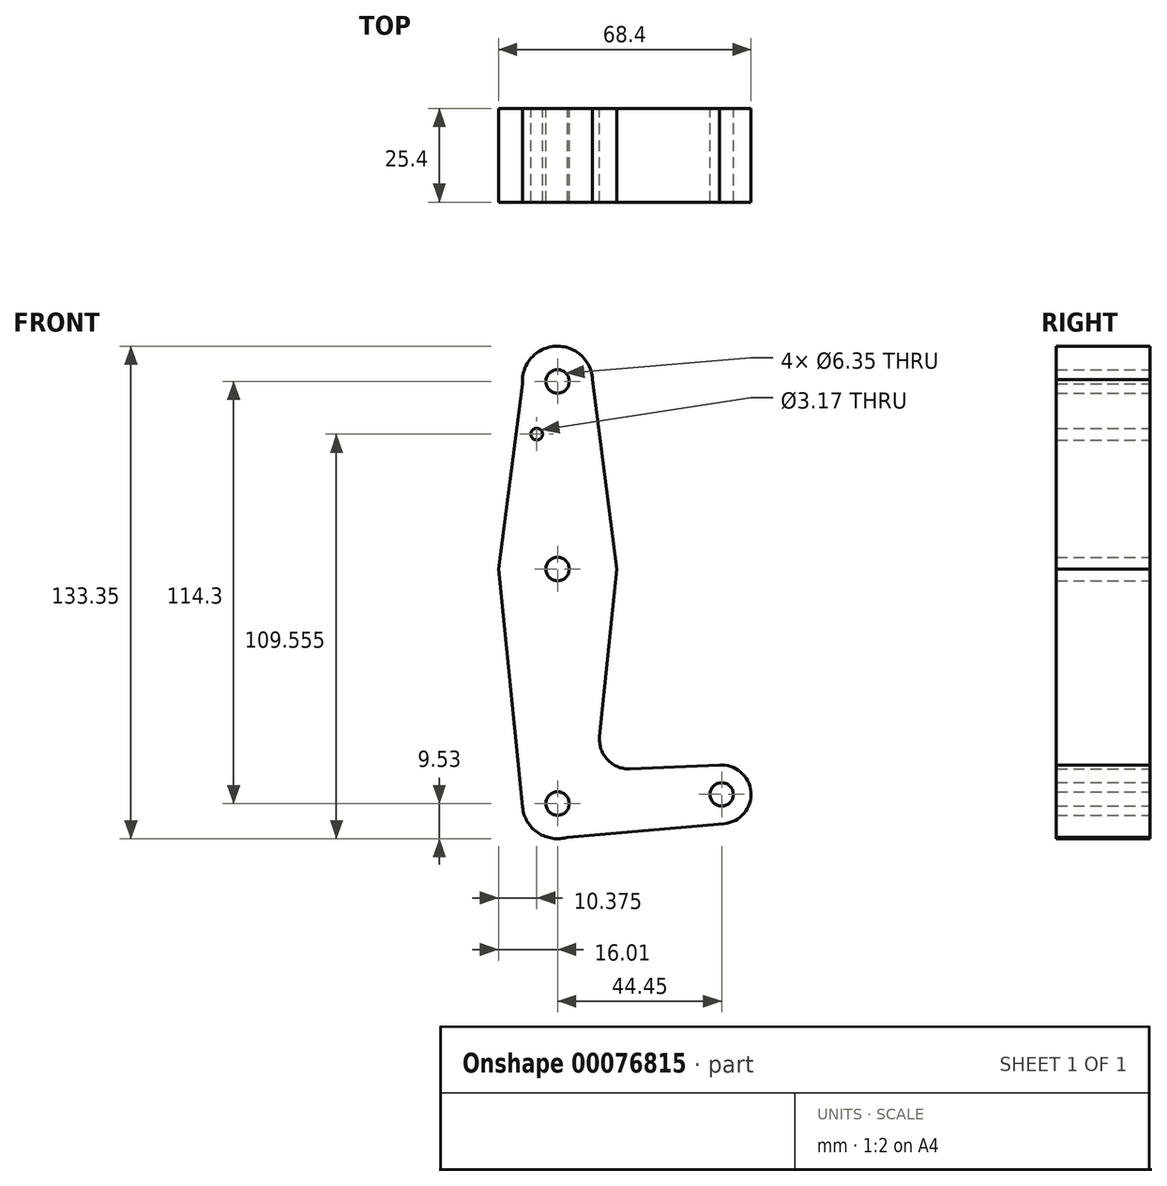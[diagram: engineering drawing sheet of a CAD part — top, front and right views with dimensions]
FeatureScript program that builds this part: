
annotation { "Feature Type Name" : "Feature", "Feature Type Description" : "" }
export const myFeature = defineFeature(function(context is Context, id is Id, definition is map)
    precondition{}
    {
        {
            var Q0;
            Q0=qCreatedBy(makeId("Front.planeOp"),FACE);
            var sketch = newSketch(context, id + "F0", { "sketchPlane" : qUnion([Q0])});
            skLineSegment(sketch, "E0", {"start": v(0, 50.8) * mm, "end": v(0, -63.5) * mm});
            skLineSegment(sketch, "E1", {"start": v(0, -63.5) * mm, "end": v(44.45, -61.03) * mm});
            skCircle(sketch, "E2", {"center": v(0, 50.8) * mm, "radius": 9.53 * mm});
            skCircle(sketch, "E3", {"center": v(0, 0) * mm, "radius": 15.88 * mm});
            skCircle(sketch, "E4", {"center": v(0, -63.5) * mm, "radius": 9.53 * mm});
            skCircle(sketch, "E5", {"center": v(44.45, -61.03) * mm, "radius": 7.94 * mm});
            skLineSegment(sketch, "E6", {"start": v(-9.5, 50.17) * mm, "end": v(-16, 0) * mm});
            skLineSegment(sketch, "E7", {"start": v(-16, 0) * mm, "end": v(-9.48, -64.46) * mm});
            skLineSegment(sketch, "E8", {"start": v(9.51, 51.33) * mm, "end": v(16, 0) * mm});
            skLineSegment(sketch, "E9", {"start": v(16, 0) * mm, "end": v(11.4, -45.37) * mm});
            skLineSegment(sketch, "E10", {"start": v(2.77, -72.61) * mm, "end": v(45.14, -68.94) * mm});
            skLineSegment(sketch, "E11", {"start": v(44.45, -53.1) * mm, "end": v(19.64, -54.11) * mm});
            skCircle(sketch, "E12", {"center": v(0, 50.8) * mm, "radius": 3.18 * mm});
            skCircle(sketch, "E13", {"center": v(-5.63, 36.53) * mm, "radius": 1.59 * mm});
            skCircle(sketch, "E14", {"center": v(0, -63.5) * mm, "radius": 3.18 * mm});
            skCircle(sketch, "E15", {"center": v(0, 0) * mm, "radius": 3.18 * mm});
            skCircle(sketch, "E16", {"center": v(44.45, -61.03) * mm, "radius": 3.18 * mm});
            skArc(sketch, "E17.filletArc", {"start": v(11.4, -45.37) * mm, "mid": v(13.53, -51.62) * mm, "end": v(19.64, -54.11) * mm});
            skSolve(sketch);
        }
        {
            var Q0;
            Q0 = qSketchRegion(id + "F0", true);
            var Q1;
            {var subQ0=sQuery(id+"F0.wireOp",EDGE,"E4");var subQ1=sQuery(id+"F0.wireOp",EDGE,"E0");var subQ2=makeQuery(id+"F0.imprint","INTERSECT",VERTEX,{"derivedFrom":[subQ1,subQ0]});Q1=makeQuery(id+"F0.imprint","IMPRINT",FACE,{"disambiguationData":[TD([[makeQuery(id+"F0.imprint","IMPRINT",EDGE,{"disambiguationData":[TD([[subQ2,-1.0]])],"derivedFrom":subQ1}),1.0]])]});}
            extrude(context, id + "F1", {"entities" : qUnion([Q0, Q1]), "depth" : 25.4 * mm});
        }
        {
            var Q0;
            Q0 = qSketchRegion(id + "F0", true);
            extrude(context, id + "F2", {"entities" : qUnion([Q0]), "operationType" : NewBodyOperationType.ADD, "depth" : 3.05 * mm});
        }
    });
